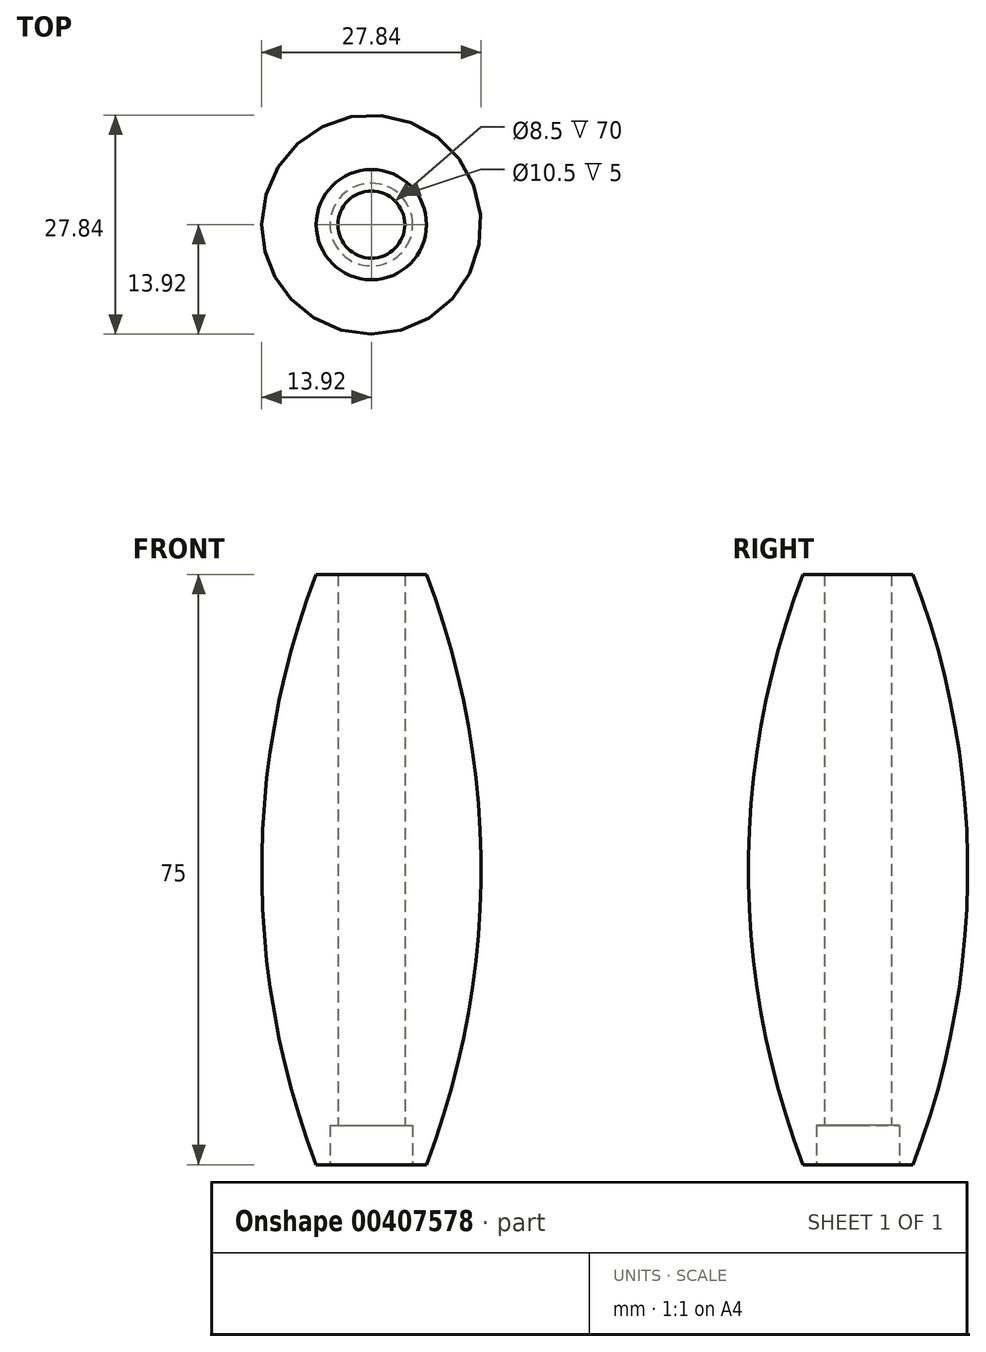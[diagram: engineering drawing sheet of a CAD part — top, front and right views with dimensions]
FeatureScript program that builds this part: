
annotation { "Feature Type Name" : "Feature", "Feature Type Description" : "" }
export const myFeature = defineFeature(function(context is Context, id is Id, definition is map)
    precondition{}
    {
        {
            var Q0;
            Q0=qCreatedBy(makeId("Front.planeOp"),FACE);
            var sketch = newSketch(context, id + "F0", { "sketchPlane" : qUnion([Q0])});
            skLineSegment(sketch, "E0", {"start": v(7, 37.5) * mm, "end": v(4.25, 37.5) * mm});
            skLineSegment(sketch, "E1", {"start": v(4.25, 37.5) * mm, "end": v(4.25, -32.5) * mm});
            skLineSegment(sketch, "E2", {"start": v(4.25, -32.5) * mm, "end": v(5.25, -32.5) * mm});
            skLineSegment(sketch, "E3", {"start": v(5.25, -32.5) * mm, "end": v(5.25, -37.5) * mm});
            skLineSegment(sketch, "E4", {"start": v(5.25, -37.5) * mm, "end": v(7, -37.5) * mm});
            skArc(sketch, "E5", {"start": v(7, -37.5) * mm, "mid": v(13.92, 0) * mm, "end": v(7, 37.5) * mm});
            skLineSegment(sketch, "E6", {"start": v(0, -59.69) * mm, "end": v(0, 60.78) * mm, "construction": true});
            skSolve(sketch);
        }
        {
            var Q0;
            Q0=makeQuery(id+"F0.imprint","IMPRINT",FACE,{"disambiguationData":[TD([[makeQuery(id+"F0.imprint","IMPRINT",EDGE,{"derivedFrom":sQuery(id+"F0.wireOp",EDGE,"E0")}),1.0]])]});
            var Q1;
            Q1=sQuery(id+"F0.wireOp",EDGE,"E6");
            revolve(context, id + "F1", {"entities" : qUnion([Q0]), "axis" : qUnion([Q1]), "revolveType" : RevolveType.FULL});
        }
    });
